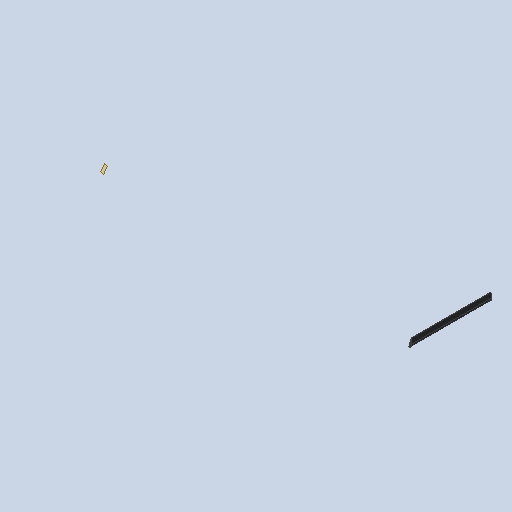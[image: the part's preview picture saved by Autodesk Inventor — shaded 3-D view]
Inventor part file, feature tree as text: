
AUTODESK INVENTOR PART (.ipt)
format: ipt  version: 2025.2 (Build 292293000, 293)  size: 102,912 bytes
history: native  units: in
note: dims shown in document units (in); Inventor stores cm internally (conversion verified against a paired STEP export)
features: other x5, reference x3, plane x2, sketch x1, extrude x1
ambient origin geometry x8: Origin, YZ Plane, XZ Plane, XY Plane, X Axis, Y Axis, Z Axis, Center Point
bodies: Solid1 (feature_tree)
feature tree (12):
  plane  "Work Plane1"
  sketch  "Sketch1"  dims[d1=1.0in d2=0.0in d3=0.5in d4=0.0344in d5=0.5in d6=0.0344in]
  plane  "Work Plane2"
  extrude  "Extrusion1"  Depth=0.5in
  reference  "Reference1"
  reference  "Reference2"
  reference  "Reference3"
  other  "<userpath>\Downloads\UAV_v0.2.0\UAV_v0.2.0\UAV_Assembly.iam"
  other  "UAV_Assembly.iam"
  other  "WingMotorPlate:1"
  other  "KST_DS215MG_MIR:1"
  other  "MiddleWingL:1"
